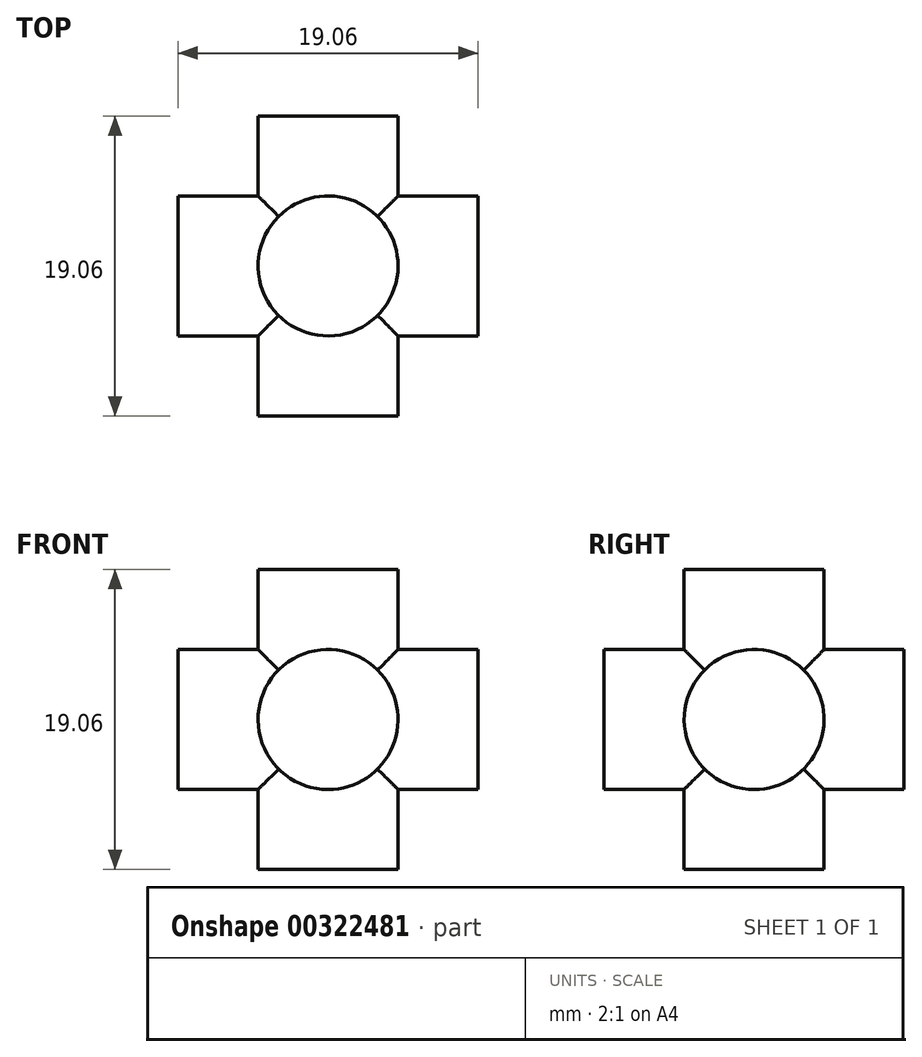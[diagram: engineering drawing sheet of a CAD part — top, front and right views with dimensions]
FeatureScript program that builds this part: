
annotation { "Feature Type Name" : "Feature", "Feature Type Description" : "" }
export const myFeature = defineFeature(function(context is Context, id is Id, definition is map)
    precondition{}
    {
        {
            var Q0;
            Q0=qCreatedBy(makeId("Front.planeOp"),FACE);
            var sketch = newSketch(context, id + "F0", { "sketchPlane" : qUnion([Q0])});
            skCircle(sketch, "E0", {"center": v(0, 0) * mm, "radius": 4.45 * mm});
            skSolve(sketch);
        }
        {
            var Q0;
            Q0=makeQuery(id+"F0.imprint","IMPRINT",FACE,{"disambiguationData":[TD([[makeQuery(id+"F0.imprint","IMPRINT",EDGE,{"derivedFrom":sQuery(id+"F0.wireOp",EDGE,"E0")}),1.0]])]});
            extrude(context, id + "F1", {"entities" : qUnion([Q0]), "endBound" : BoundingType.SYMMETRIC, "depth" : 19.05 * mm});
        }
        {
            var Q0;
            Q0=qCreatedBy(makeId("Right.planeOp"),FACE);
            var sketch = newSketch(context, id + "F2", { "sketchPlane" : qUnion([Q0])});
            skCircle(sketch, "E1", {"center": v(0, 0) * mm, "radius": 4.45 * mm});
            skSolve(sketch);
        }
        {
            var Q0;
            Q0 = qSketchRegion(id + "F2", true);
            extrude(context, id + "F3", {"entities" : qUnion([Q0]), "operationType" : NewBodyOperationType.ADD, "endBound" : BoundingType.SYMMETRIC, "depth" : 19.05 * mm});
        }
        {
            var Q0;
            Q0=qCreatedBy(makeId("Top.planeOp"),FACE);
            var sketch = newSketch(context, id + "F4", { "sketchPlane" : qUnion([Q0])});
            skCircle(sketch, "E2", {"center": v(0, 0) * mm, "radius": 4.45 * mm});
            skSolve(sketch);
        }
        {
            var Q0;
            Q0 = qSketchRegion(id + "F4", true);
            extrude(context, id + "F5", {"entities" : qUnion([Q0]), "operationType" : NewBodyOperationType.ADD, "endBound" : BoundingType.SYMMETRIC, "depth" : 19.05 * mm});
        }
    });
